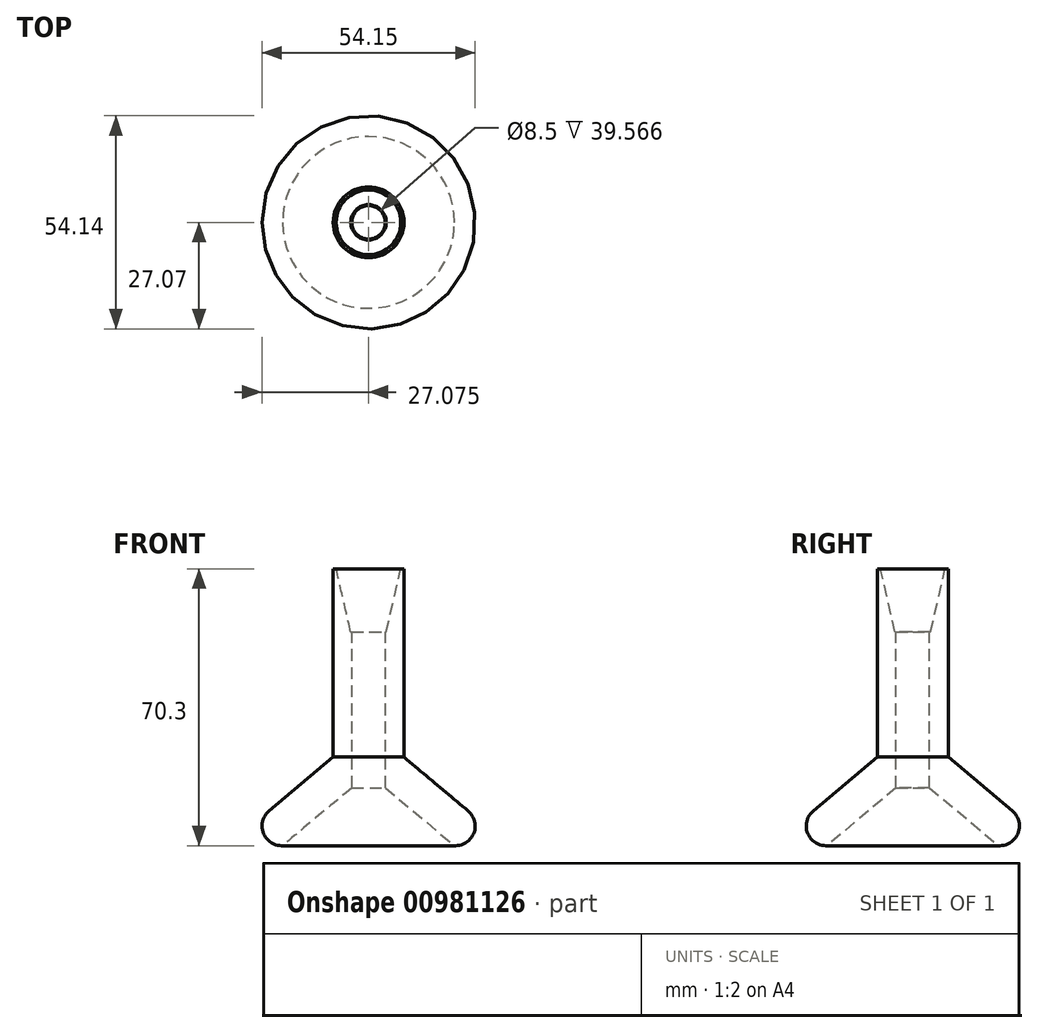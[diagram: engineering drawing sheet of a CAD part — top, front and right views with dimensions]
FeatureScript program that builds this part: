
annotation { "Feature Type Name" : "Feature", "Feature Type Description" : "" }
export const myFeature = defineFeature(function(context is Context, id is Id, definition is map)
    precondition{}
    {
        {
            var Q0;
            Q0=qCreatedBy(makeId("Front.planeOp"),FACE);
            var sketch = newSketch(context, id + "F0", { "sketchPlane" : qUnion([Q0])});
            skLineSegment(sketch, "E0", {"start": v(-9.78, 51.5) * mm, "end": v(-9.78, 3.7) * mm});
            skLineSegment(sketch, "E1.1", {"start": v(-0.78, 51.5) * mm, "end": v(-0.78, 1.83) * mm});
            skLineSegment(sketch, "E2", {"start": v(-9.78, 51.5) * mm, "end": v(-0.78, 51.5) * mm});
            skLineSegment(sketch, "E3", {"start": v(-9.78, 3.7) * mm, "end": v(-36.6, -18.8) * mm});
            skLineSegment(sketch, "E4", {"start": v(-36.6, -18.8) * mm, "end": v(-22.6, -18.8) * mm});
            skLineSegment(sketch, "E5", {"start": v(-22.6, -18.8) * mm, "end": v(-2.57, -2) * mm});
            skPoint(sketch, "E6.visualSharp", {"position": v(-0.78, -0.5) * mm});
            skArc(sketch, "E6.filletArc", {"start": v(-2.57, -2) * mm, "mid": v(-1.25, -0.28) * mm, "end": v(-0.78, 1.83) * mm});
            skSolve(sketch);
        }
        {
            var Q0;
            Q0 = qSketchRegion(id + "F0", true);
            var Q1;
            Q1=sQuery(id+"F0.wireOp",EDGE,"E1.1");
            revolve(context, id + "F1", {"surfaceOperationType" : NewSurfaceOperationType.NEW, "entities" : qUnion([Q0]), "axis" : qUnion([Q1]), "revolveType" : RevolveType.FULL});
        }
        {
            var Q0;
            Q0=makeQuery(id+"F1.opRevolve","SWEPT_EDGE",EDGE,{"disambiguationData":[OSD([sQuery(id+"F0.wireOp",EDGE,"E3"),sQuery(id+"F0.wireOp",EDGE,"E4")])]});
            fillet(context, id + "F2", {"entities" : qUnion([Q0]), "radius" : 5 * mm, "tangentPropagation" : true, "allowEdgeOverflow" : false});
        }
        {
            var Q0;
            Q0=makeQuery(id+"F1.opRevolve","SWEPT_FACE",FACE,{"disambiguationData":[OSD([sQuery(id+"F0.wireOp",EDGE,"E2")])]});
            var sketch = newSketch(context, id + "F3", { "sketchPlane" : qUnion([Q0])});
            skCircle(sketch, "E7", {"center": v(-0.78, 0) * mm, "radius": 4.25 * mm});
            skSolve(sketch);
        }
        {
            var Q0;
            Q0 = qSketchRegion(id + "F3", true);
            extrude(context, id + "F4", {"entities" : qUnion([Q0]), "operationType" : NewBodyOperationType.REMOVE, "oppositeDirection" : true, "depth" : 70 * mm, "offsetDistance" : 25 * mm});
        }
        {
            var Q0;
            Q0=qCreatedBy(makeId("Front.planeOp"),FACE);
            var sketch = newSketch(context, id + "F5", { "sketchPlane" : qUnion([Q0])});
            skLineSegment(sketch, "E8", {"start": v(-0.8, 51.5) * mm, "end": v(-0.8, 35.5) * mm});
            skLineSegment(sketch, "E9", {"start": v(-0.8, 35.5) * mm, "end": v(3.7, 35.5) * mm});
            skLineSegment(sketch, "E10", {"start": v(3.7, 35.5) * mm, "end": v(7.4, 51.5) * mm});
            skLineSegment(sketch, "E11", {"start": v(7.4, 51.5) * mm, "end": v(-0.8, 51.5) * mm});
            skSolve(sketch);
        }
        {
            var Q0;
            Q0 = qSketchRegion(id + "F5", true);
            var Q1;
            Q1=sQuery(id+"F5.wireOp",EDGE,"E8");
            revolve(context, id + "F6", {"operationType" : NewBodyOperationType.REMOVE, "surfaceOperationType" : NewSurfaceOperationType.NEW, "entities" : qUnion([Q0]), "axis" : qUnion([Q1]), "revolveType" : RevolveType.FULL, "oppositeDirection" : true});
        }
    });
